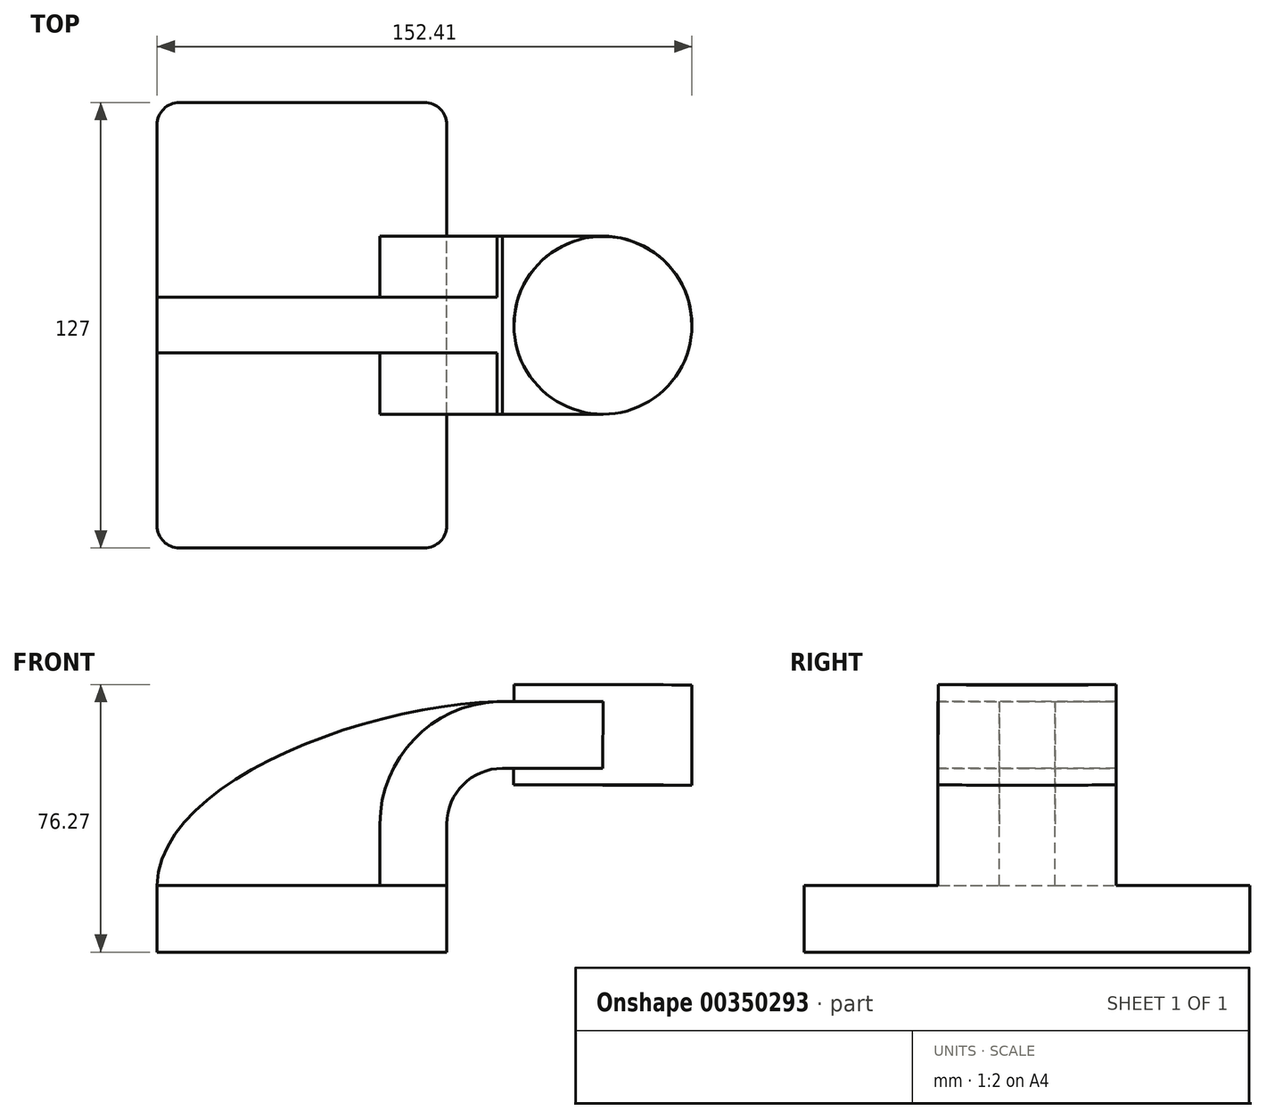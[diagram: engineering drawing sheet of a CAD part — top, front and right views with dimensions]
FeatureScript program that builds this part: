
annotation { "Feature Type Name" : "Feature", "Feature Type Description" : "" }
export const myFeature = defineFeature(function(context is Context, id is Id, definition is map)
    precondition{}
    {
        {
            var Q0;
            Q0=qCreatedBy(makeId("Front.planeOp"),FACE);
            var sketch = newSketch(context, id + "F0", { "sketchPlane" : qUnion([Q0])});
            skLineSegment(sketch, "E0.bottom", {"start": v(-41.28, -9.53) * mm, "end": v(41.28, -9.53) * mm});
            skLineSegment(sketch, "E0.top", {"start": v(-41.28, 9.53) * mm, "end": v(41.28, 9.53) * mm});
            skLineSegment(sketch, "E0.left", {"start": v(-41.27, -9.53) * mm, "end": v(-41.28, 9.53) * mm});
            skLineSegment(sketch, "E0.right", {"start": v(41.28, -9.53) * mm, "end": v(41.28, 9.53) * mm});
            skPoint(sketch, "E0.middle", {"position": v(0, 0) * mm});
            skLineSegment(sketch, "E1.bottom", {"start": v(60.32, 38.1) * mm, "end": v(111.12, 38.1) * mm});
            skLineSegment(sketch, "E1.top", {"start": v(60.32, 66.67) * mm, "end": v(111.12, 66.67) * mm});
            skLineSegment(sketch, "E1.left", {"start": v(60.32, 38.1) * mm, "end": v(60.32, 66.67) * mm});
            skLineSegment(sketch, "E1.right", {"start": v(111.12, 38.1) * mm, "end": v(111.12, 66.67) * mm});
            skPoint(sketch, "E1.middle", {"position": v(85.72, 52.39) * mm});
            skLineSegment(sketch, "E2", {"start": v(41.27, 9.52) * mm, "end": v(41.27, 27) * mm});
            skArc(sketch, "E3", {"start": v(41.27, 27) * mm, "mid": v(45.92, 38.23) * mm, "end": v(57.15, 42.88) * mm});
            skLineSegment(sketch, "E4", {"start": v(57.15, 42.88) * mm, "end": v(85.8, 42.88) * mm});
            skLineSegment(sketch, "E5.0", {"start": v(57.15, 61.93) * mm, "end": v(85.76, 61.93) * mm});
            skArc(sketch, "E5.1", {"start": v(22.22, 27) * mm, "mid": v(32.45, 51.7) * mm, "end": v(57.15, 61.93) * mm});
            skLineSegment(sketch, "E5.2", {"start": v(22.22, 9.52) * mm, "end": v(22.22, 27) * mm});
            skPoint(sketch, "E6.positionSnap0", {"position": v(85.72, 38.1) * mm});
            skLineSegment(sketch, "E7", {"start": v(85.72, 38.1) * mm, "end": v(85.76, 66.67) * mm});
            skFitSpline(sketch, "E8", {"points": [v(-41.28, 9.52) * mm, v(57.15, 61.93) * mm], "startDerivative": vector(1.55, 89.02) * mm, "endDerivative": vector(115.3, 1.67) * mm});
            skSolve(sketch);
        }
        {
            var Q0;
            Q0=makeQuery(id+"F0.imprint","IMPRINT",FACE,{"disambiguationData":[TD([[makeQuery(id+"F0.imprint","IMPRINT",EDGE,{"derivedFrom":sQuery(id+"F0.wireOp",EDGE,"E0.bottom")}),1.0]])]});
            extrude(context, id + "F1", {"entities" : qUnion([Q0]), "endBound" : BoundingType.SYMMETRIC, "depth" : 127 * mm});
        }
        {
            var Q0;
            {var subQ1=sQuery(id+"F0.wireOp",EDGE,"E2");Q0=makeQuery(id+"F0.imprint","IMPRINT",FACE,{"disambiguationData":[TD([[makeQuery(id+"F0.imprint","IMPRINT",EDGE,{"derivedFrom":subQ1}),1.0]])]});}
            var Q1;
            {var subQ0=sQuery(id+"F0.wireOp",EDGE,"E4");var subQ1=sQuery(id+"F0.wireOp",EDGE,"E1.left");var subQ2=makeQuery(id+"F0.imprint","INTERSECT",VERTEX,{"derivedFrom":[subQ1,subQ0]});Q1=makeQuery(id+"F0.imprint","IMPRINT",FACE,{"disambiguationData":[TD([[makeQuery(id+"F0.imprint","IMPRINT",EDGE,{"disambiguationData":[TD([[subQ2,-1.0]])],"derivedFrom":subQ1}),-1.0]])]});}
            extrude(context, id + "F2", {"entities" : qUnion([Q0, Q1]), "operationType" : NewBodyOperationType.ADD, "endBound" : BoundingType.SYMMETRIC, "depth" : 50.8 * mm});
        }
        {
            var Q0;
            {var subQ3=sQuery(id+"F0.wireOp",EDGE,"E5.2");Q0=makeQuery(id+"F0.imprint","IMPRINT",FACE,{"disambiguationData":[TD([[makeQuery(id+"F0.imprint","IMPRINT",EDGE,{"derivedFrom":subQ3}),1.0]])]});}
            extrude(context, id + "F3", {"entities" : qUnion([Q0]), "operationType" : NewBodyOperationType.ADD, "endBound" : BoundingType.SYMMETRIC, "depth" : 15.88 * mm});
        }
        {
            var Q0;
            {var subQ4=sQuery(id+"F0.wireOp",EDGE,"E1.right");Q0=makeQuery(id+"F0.imprint","IMPRINT",FACE,{"disambiguationData":[TD([[makeQuery(id+"F0.imprint","IMPRINT",EDGE,{"derivedFrom":subQ4}),1.0]])]});}
            var Q1;
            Q1=sQuery(id+"F0.wireOp",EDGE,"E7");
            revolve(context, id + "F4", {"operationType" : NewBodyOperationType.ADD, "entities" : qUnion([Q0]), "axis" : qUnion([Q1]), "revolveType" : RevolveType.FULL});
        }
        {
            var Q0;
            Q0=makeQuery(id+"F1.opExtrude","CAP_EDGE",EDGE,{"disambiguationData":[OSD([sQuery(id+"F0.wireOp",EDGE,"E0.right")])],"isStart":false});
            var Q1;
            Q1=makeQuery(id+"F1.opExtrude","CAP_EDGE",EDGE,{"disambiguationData":[OSD([sQuery(id+"F0.wireOp",EDGE,"E0.left")])],"isStart":false});
            var Q2;
            Q2=makeQuery(id+"F1.opExtrude","CAP_EDGE",EDGE,{"disambiguationData":[OSD([sQuery(id+"F0.wireOp",EDGE,"E0.left")])],"isStart":true});
            var Q3;
            Q3=makeQuery(id+"F1.opExtrude","CAP_EDGE",EDGE,{"disambiguationData":[OSD([sQuery(id+"F0.wireOp",EDGE,"E0.right")])],"isStart":true});
            fillet(context, id + "F5", {"entities" : qUnion([Q0, Q1, Q2, Q3]), "radius" : 6.35 * mm, "tangentPropagation" : true, "allowEdgeOverflow" : false});
        }
    });
